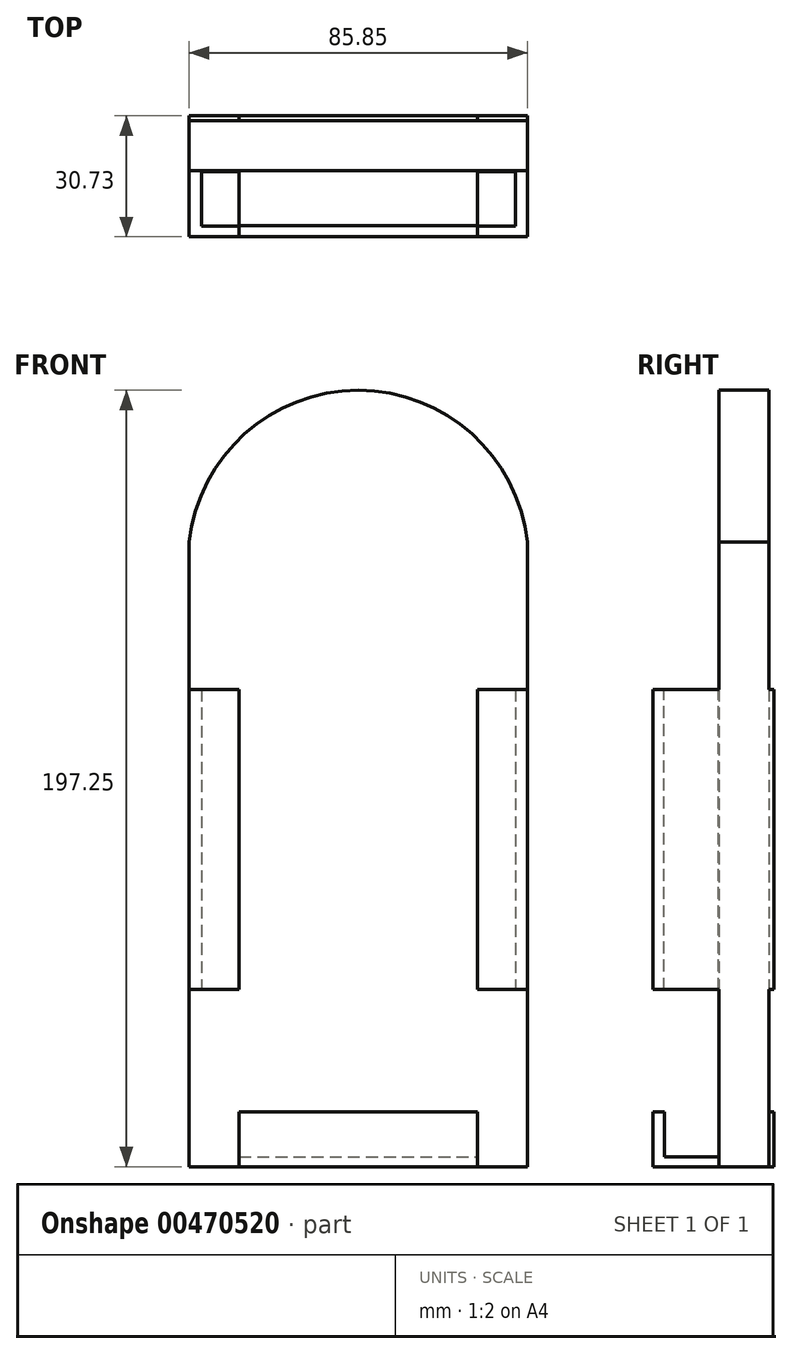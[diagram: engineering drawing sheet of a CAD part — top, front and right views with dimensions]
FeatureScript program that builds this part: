
annotation { "Feature Type Name" : "Feature", "Feature Type Description" : "" }
export const myFeature = defineFeature(function(context is Context, id is Id, definition is map)
    precondition{}
    {
        {
            var Q0;
            Q0=qCreatedBy(makeId("Front.planeOp"),FACE);
            var sketch = newSketch(context, id + "F0", { "sketchPlane" : qUnion([Q0])});
            skLineSegment(sketch, "E0.bottom", {"start": v(51.35, -59.13) * mm, "end": v(-34.5, -59.13) * mm});
            skLineSegment(sketch, "E0.top", {"start": v(51.35, 99.62) * mm, "end": v(-34.5, 99.62) * mm});
            skLineSegment(sketch, "E0.left", {"start": v(51.35, -59.13) * mm, "end": v(51.35, 99.62) * mm});
            skLineSegment(sketch, "E0.right", {"start": v(-34.5, -59.13) * mm, "end": v(-34.5, 99.62) * mm});
            skLineSegment(sketch, "E1.bottom", {"start": v(-34.5, 62.08) * mm, "end": v(-21.8, 62.08) * mm});
            skLineSegment(sketch, "E1.top", {"start": v(-34.5, -14.12) * mm, "end": v(-21.8, -14.12) * mm});
            skLineSegment(sketch, "E1.left", {"start": v(-34.5, 62.08) * mm, "end": v(-34.5, -14.12) * mm});
            skLineSegment(sketch, "E1.right", {"start": v(-21.8, 62.08) * mm, "end": v(-21.8, -14.12) * mm});
            skLineSegment(sketch, "E2.left", {"start": v(-34.5, 69.9) * mm, "end": v(-34.5, -20.32) * mm});
            skLineSegment(sketch, "E3", {"start": v(51.35, 62.08) * mm, "end": v(38.65, 62.08) * mm});
            skLineSegment(sketch, "E4", {"start": v(38.65, 62.08) * mm, "end": v(38.65, -14.12) * mm});
            skLineSegment(sketch, "E5", {"start": v(38.65, -14.12) * mm, "end": v(51.35, -14.12) * mm});
            skLineSegment(sketch, "E6.left", {"start": v(51.35, 68.24) * mm, "end": v(51.35, -21.04) * mm});
            skLineSegment(sketch, "E7.bottom", {"start": v(-21.8, -59.13) * mm, "end": v(38.65, -59.13) * mm});
            skLineSegment(sketch, "E7.top", {"start": v(-21.8, -45.15) * mm, "end": v(38.65, -45.15) * mm});
            skLineSegment(sketch, "E7.left", {"start": v(-21.8, -59.13) * mm, "end": v(-21.8, -45.15) * mm});
            skLineSegment(sketch, "E7.right", {"start": v(38.65, -59.13) * mm, "end": v(38.65, -45.15) * mm});
            skLineSegment(sketch, "E8.bottom", {"start": v(-30.73, -59.13) * mm, "end": v(35.63, -59.13) * mm});
            skArc(sketch, "E9", {"start": v(51.35, 99.62) * mm, "mid": v(8.43, 138.12) * mm, "end": v(-34.5, 99.62) * mm});
            skSolve(sketch);
        }
        {
            var Q0;
            {var subQ4=sQuery(id+"F0.wireOp",EDGE,"E0.top");Q0=makeQuery(id+"F0.imprint","IMPRINT",FACE,{"disambiguationData":[TD([[makeQuery(id+"F0.imprint","IMPRINT",EDGE,{"derivedFrom":subQ4}),1.0]])]});}
            var Q1;
            Q1=makeQuery(id+"F0.imprint","IMPRINT",FACE,{"disambiguationData":[TD([[makeQuery(id+"F0.imprint","IMPRINT",EDGE,{"derivedFrom":sQuery(id+"F0.wireOp",EDGE,"E0.top")}),-1.0]])]});
            extrude(context, id + "F1", {"entities" : qUnion([Q0, Q1]), "endBound" : BoundingType.SYMMETRIC, "depth" : 12.7 * mm, "offsetDistance" : 25.4 * mm});
        }
        {
            var Q0;
            {var subQ0=sQuery(id+"F0.wireOp",EDGE,"E1.bottom");Q0=makeQuery(id+"F0.imprint","IMPRINT",FACE,{"disambiguationData":[TD([[makeQuery(id+"F0.imprint","IMPRINT",EDGE,{"derivedFrom":subQ0}),-1.0]])]});}
            var Q1;
            {var subQ0=sQuery(id+"F0.wireOp",EDGE,"E3");Q1=makeQuery(id+"F0.imprint","IMPRINT",FACE,{"disambiguationData":[TD([[makeQuery(id+"F0.imprint","IMPRINT",EDGE,{"derivedFrom":subQ0}),1.0]])]});}
            var Q2;
            Q2=makeQuery(id+"F0.imprint","IMPRINT",FACE,{"disambiguationData":[TD([[makeQuery(id+"F0.imprint","IMPRINT",EDGE,{"derivedFrom":sQuery(id+"F0.wireOp",EDGE,"E7.top")}),-1.0]])]});
            extrude(context, id + "F2", {"entities" : qUnion([Q0, Q1, Q2]), "operationType" : NewBodyOperationType.ADD, "depth" : 23.1 * mm, "hasSecondDirection" : true, "secondDirectionOppositeDirection" : true, "secondDirectionDepth" : 7.62 * mm});
        }
        {
            var Q0;
            {var subQ0=sQuery(id+"F0.wireOp",EDGE,"E2.left");var subQ1=sQuery(id+"F0.wireOp",EDGE,"E1.right");var subQ2=sQuery(id+"F0.wireOp",EDGE,"E1.top");var subQ3=sQuery(id+"F0.wireOp",EDGE,"E1.bottom");Q0=makeQuery(id+"F2.boolean.opBoolean","SPLIT",FACE,{"disambiguationData":[TD([makeQuery(id+"F2.opExtrude","CAP_FACE",FACE,{"disambiguationData":[OSD([subQ3,subQ2,subQ1,subQ0])],"isStart":false})])],"derivedFrom":makeQuery(id+"F2.opExtrude","SWEPT_FACE",FACE,{"disambiguationData":[OSD([subQ1])]})});}
            var sketch = newSketch(context, id + "F3", { "sketchPlane" : qUnion([Q0])});
            skLineSegment(sketch, "E10.bottom", {"start": v(-20.43, 63.98) * mm, "end": v(-6.58, 63.98) * mm});
            skLineSegment(sketch, "E10.top", {"start": v(-20.43, -17.75) * mm, "end": v(-6.58, -17.75) * mm});
            skLineSegment(sketch, "E10.left", {"start": v(-20.43, 63.98) * mm, "end": v(-20.43, -17.75) * mm});
            skLineSegment(sketch, "E10.right", {"start": v(-6.58, 63.98) * mm, "end": v(-6.58, -17.75) * mm});
            skSolve(sketch);
        }
        {
            var Q0;
            Q0 = qSketchRegion(id + "F3", true);
            extrude(context, id + "F4", {"entities" : qUnion([Q0]), "operationType" : NewBodyOperationType.REMOVE, "depth" : 70.1 * mm, "hasSecondDirection" : true, "secondDirectionOppositeDirection" : true, "secondDirectionDepth" : 9.65 * mm});
        }
        {
            var Q0;
            {var subQ0=sQuery(id+"F0.wireOp",EDGE,"E8.bottom");var subQ1=sQuery(id+"F0.wireOp",EDGE,"E7.right");var subQ2=sQuery(id+"F0.wireOp",EDGE,"E7.left");var subQ3=sQuery(id+"F0.wireOp",EDGE,"E7.top");Q0=makeQuery(id+"F2.boolean.opBoolean","SPLIT",FACE,{"disambiguationData":[TD([makeQuery(id+"F2.opExtrude","CAP_FACE",FACE,{"disambiguationData":[OSD([sQuery(id+"F0.wireOp",EDGE,"E7.bottom"),subQ3,subQ2,subQ1,subQ0])],"isStart":false})])],"derivedFrom":makeQuery(id+"F2.opExtrude","SWEPT_FACE",FACE,{"disambiguationData":[OSD([subQ3])]})});}
            var sketch = newSketch(context, id + "F5", { "sketchPlane" : qUnion([Q0])});
            skLineSegment(sketch, "E11.bottom", {"start": v(-21.8, -6.35) * mm, "end": v(38.65, -6.35) * mm});
            skLineSegment(sketch, "E11.top", {"start": v(-21.8, -20.3) * mm, "end": v(38.65, -20.3) * mm});
            skLineSegment(sketch, "E11.left", {"start": v(-21.8, -6.35) * mm, "end": v(-21.8, -20.3) * mm});
            skLineSegment(sketch, "E11.right", {"start": v(38.65, -6.35) * mm, "end": v(38.65, -20.3) * mm});
            skSolve(sketch);
        }
        {
            var Q0;
            Q0 = qSketchRegion(id + "F5", true);
            extrude(context, id + "F6", {"entities" : qUnion([Q0]), "operationType" : NewBodyOperationType.REMOVE, "oppositeDirection" : true, "depth" : 11.43 * mm, "offsetDistance" : 25.4 * mm});
        }
    });
